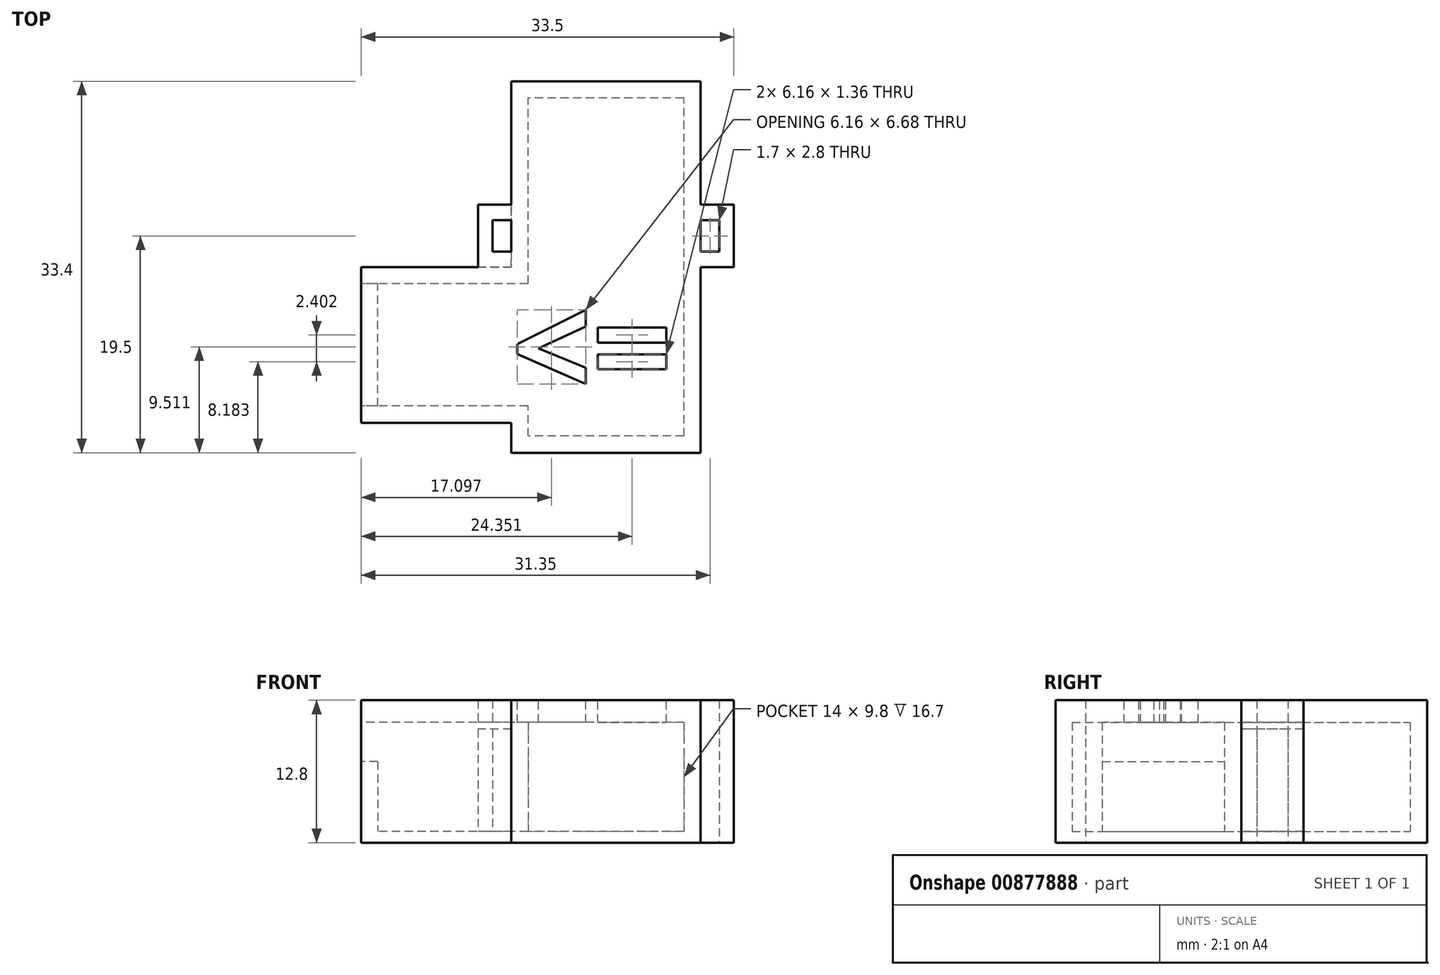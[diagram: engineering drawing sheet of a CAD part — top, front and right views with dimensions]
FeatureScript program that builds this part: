
annotation { "Feature Type Name" : "Feature", "Feature Type Description" : "" }
export const myFeature = defineFeature(function(context is Context, id is Id, definition is map)
    precondition{}
    {
        {
            var Q0;
            Q0=qCreatedBy(makeId("Top.planeOp"),FACE);
            var sketch = newSketch(context, id + "F0", { "sketchPlane" : qUnion([Q0])});
            skLineSegment(sketch, "E0.bottom", {"start": v(7, -15.2) * mm, "end": v(-7, -15.2) * mm});
            skLineSegment(sketch, "E0.top", {"start": v(7, 15.2) * mm, "end": v(-7, 15.2) * mm});
            skLineSegment(sketch, "E0.left", {"start": v(7, -15.2) * mm, "end": v(7, 15.2) * mm});
            skLineSegment(sketch, "E0.right", {"start": v(-7, -15.2) * mm, "end": v(-7, -12.5) * mm});
            skPoint(sketch, "E0.middle", {"position": v(0, 0) * mm});
            skLineSegment(sketch, "E1.bottom", {"start": v(-7, -12.5) * mm, "end": v(-20.5, -12.5) * mm});
            skLineSegment(sketch, "E1.top", {"start": v(-7, -1.5) * mm, "end": v(-20.5, -1.5) * mm});
            skLineSegment(sketch, "E1.right", {"start": v(-20.5, -12.5) * mm, "end": v(-20.5, -1.5) * mm});
            skLineSegment(sketch, "E2.trimOffspring", {"start": v(-7, -1.5) * mm, "end": v(-7, 15.2) * mm});
            skLineSegment(sketch, "E3.0", {"start": v(-8.5, 0) * mm, "end": v(-22, 0) * mm});
            skLineSegment(sketch, "E3.1", {"start": v(-22, -14) * mm, "end": v(-22, 0) * mm});
            skLineSegment(sketch, "E3.2", {"start": v(-8.5, 0) * mm, "end": v(-8.5, 16.7) * mm});
            skLineSegment(sketch, "E3.3", {"start": v(-8.5, -14) * mm, "end": v(-22, -14) * mm});
            skLineSegment(sketch, "E3.4", {"start": v(8.5, 16.7) * mm, "end": v(-8.5, 16.7) * mm});
            skLineSegment(sketch, "E3.5", {"start": v(8.5, -16.7) * mm, "end": v(8.5, 16.7) * mm});
            skLineSegment(sketch, "E3.6", {"start": v(8.5, -16.7) * mm, "end": v(-8.5, -16.7) * mm});
            skLineSegment(sketch, "E3.7", {"start": v(-8.5, -16.7) * mm, "end": v(-8.5, -14) * mm});
            skLineSegment(sketch, "E4.0", {"start": v(-7.75, -0.75) * mm, "end": v(-21.25, -0.75) * mm});
            skLineSegment(sketch, "E4.1", {"start": v(-21.25, -13.25) * mm, "end": v(-21.25, -0.75) * mm});
            skLineSegment(sketch, "E4.2", {"start": v(-7.75, -0.75) * mm, "end": v(-7.75, 15.95) * mm});
            skLineSegment(sketch, "E4.3", {"start": v(-7.75, -13.25) * mm, "end": v(-21.25, -13.25) * mm});
            skLineSegment(sketch, "E4.4", {"start": v(7.75, 15.95) * mm, "end": v(-7.75, 15.95) * mm});
            skLineSegment(sketch, "E4.5", {"start": v(7.75, -15.95) * mm, "end": v(7.75, 15.95) * mm});
            skLineSegment(sketch, "E4.6", {"start": v(7.75, -15.95) * mm, "end": v(-7.75, -15.95) * mm});
            skLineSegment(sketch, "E4.7", {"start": v(-7.75, -15.95) * mm, "end": v(-7.75, -13.25) * mm});
            skLineSegment(sketch, "E5.0", {"start": v(-8.5, 0) * mm, "end": v(-11.5, 0) * mm});
            skLineSegment(sketch, "E5.1", {"start": v(-11.5, 5.6) * mm, "end": v(-11.5, 0) * mm});
            skLineSegment(sketch, "E5.2", {"start": v(-8.5, 5.6) * mm, "end": v(-11.5, 5.6) * mm});
            skLineSegment(sketch, "E5.3", {"start": v(-8.5, 4.2) * mm, "end": v(-8.5, 5.6) * mm});
            skLineSegment(sketch, "E5.4", {"start": v(-8.5, 4.2) * mm, "end": v(-10.2, 4.2) * mm});
            skLineSegment(sketch, "E5.5", {"start": v(-10.2, 4.2) * mm, "end": v(-10.2, 1.4) * mm});
            skLineSegment(sketch, "E5.6", {"start": v(-8.5, 1.4) * mm, "end": v(-10.2, 1.4) * mm});
            skLineSegment(sketch, "E5.7", {"start": v(-8.5, 0) * mm, "end": v(-8.5, 1.4) * mm});
            skLineSegment(sketch, "E6.MirrorCS", {"start": v(8.5, 4.2) * mm, "end": v(10.2, 4.2) * mm});
            skLineSegment(sketch, "E7.MirrorCS", {"start": v(10.2, 4.2) * mm, "end": v(10.2, 1.4) * mm});
            skLineSegment(sketch, "E8.MirrorCS", {"start": v(8.5, 1.4) * mm, "end": v(10.2, 1.4) * mm});
            skLineSegment(sketch, "E9.MirrorCS", {"start": v(11.5, 5.6) * mm, "end": v(11.5, 0) * mm});
            skLineSegment(sketch, "E10.MirrorCS", {"start": v(8.5, 5.6) * mm, "end": v(11.5, 5.6) * mm});
            skLineSegment(sketch, "E11", {"start": v(11.5, 0) * mm, "end": v(8.5, 0) * mm});
            skSolve(sketch);
        }
        {
            var Q0;
            Q0 = qSketchRegion(id + "F0", true);
            var Q1;
            Q1=makeQuery(id+"F0.imprint","IMPRINT",FACE,{"disambiguationData":[TD([[makeQuery(id+"F0.imprint","IMPRINT",EDGE,{"derivedFrom":sQuery(id+"F0.wireOp",EDGE,"E0.bottom")}),1.0]])]});
            extrude(context, id + "F1", {"entities" : qUnion([Q0, Q1]), "depth" : 9.2 * mm, "offsetDistance" : 25 * mm});
        }
        {
            var Q0;
            Q0=makeQuery(id+"F0.imprint","IMPRINT",FACE,{"disambiguationData":[TD([[makeQuery(id+"F0.imprint","IMPRINT",EDGE,{"derivedFrom":sQuery(id+"F0.wireOp",EDGE,"E0.bottom")}),-1.0]])]});
            var Q1;
            Q1=makeQuery(id+"F0.imprint","IMPRINT",FACE,{"disambiguationData":[TD([[makeQuery(id+"F0.imprint","IMPRINT",EDGE,{"derivedFrom":sQuery(id+"F0.wireOp",EDGE,"E0.bottom")}),1.0]])]});
            var Q2;
            Q2=makeQuery(id+"F0.imprint","IMPRINT",FACE,{"disambiguationData":[TD([[makeQuery(id+"F0.imprint","IMPRINT",EDGE,{"derivedFrom":sQuery(id+"F0.wireOp",EDGE,"E3.0")}),1.0]])]});
            extrude(context, id + "F2", {"entities" : qUnion([Q0, Q1, Q2]), "operationType" : NewBodyOperationType.ADD, "oppositeDirection" : true, "depth" : 1 * mm, "offsetDistance" : 25 * mm});
        }
        {
            var Q0;
            Q0=makeQuery(id+"F0.imprint","IMPRINT",FACE,{"disambiguationData":[TD([[makeQuery(id+"F0.imprint","IMPRINT",EDGE,{"derivedFrom":sQuery(id+"F0.wireOp",EDGE,"E3.0")}),1.0]])]});
            var Q1;
            {var subQ0=sQuery(id+"F0.wireOp",EDGE,"E6.MirrorCS");Q1=makeQuery(id+"F0.imprint","IMPRINT",FACE,{"disambiguationData":[TD([[makeQuery(id+"F0.imprint","IMPRINT",EDGE,{"derivedFrom":subQ0}),1.0]])]});}
            var Q2;
            Q2=makeQuery(id+"F0.imprint","IMPRINT",FACE,{"disambiguationData":[TD([[makeQuery(id+"F0.imprint","IMPRINT",EDGE,{"derivedFrom":sQuery(id+"F0.wireOp",EDGE,"E5.0")}),-1.0]])]});
            extrude(context, id + "F3", {"entities" : qUnion([Q0, Q1, Q2]), "operationType" : NewBodyOperationType.ADD, "depth" : 9.8 * mm, "offsetDistance" : 25 * mm});
        }
        {
            var Q0;
            Q0=makeQuery(id+"F1.opExtrude","CAP_FACE",FACE,{"disambiguationData":[OSD([sQuery(id+"F0.wireOp",EDGE,"E0.bottom"),sQuery(id+"F0.wireOp",EDGE,"E0.top"),sQuery(id+"F0.wireOp",EDGE,"E0.left"),sQuery(id+"F0.wireOp",EDGE,"E0.right"),sQuery(id+"F0.wireOp",EDGE,"E1.bottom"),sQuery(id+"F0.wireOp",EDGE,"E1.top"),sQuery(id+"F0.wireOp",EDGE,"E1.right"),sQuery(id+"F0.wireOp",EDGE,"E2.trimOffspring"),sQuery(id+"F0.wireOp",EDGE,"E3.0"),sQuery(id+"F0.wireOp",EDGE,"E3.1"),sQuery(id+"F0.wireOp",EDGE,"E3.2"),sQuery(id+"F0.wireOp",EDGE,"E3.3"),sQuery(id+"F0.wireOp",EDGE,"E3.4"),sQuery(id+"F0.wireOp",EDGE,"E3.5"),sQuery(id+"F0.wireOp",EDGE,"E3.6"),sQuery(id+"F0.wireOp",EDGE,"E3.7"),sQuery(id+"F0.wireOp",EDGE,"E5.1"),sQuery(id+"F0.wireOp",EDGE,"E5.2"),sQuery(id+"F0.wireOp",EDGE,"E5.4"),sQuery(id+"F0.wireOp",EDGE,"E5.5"),sQuery(id+"F0.wireOp",EDGE,"E5.6"),sQuery(id+"F0.wireOp",EDGE,"E6.MirrorCS"),sQuery(id+"F0.wireOp",EDGE,"E7.MirrorCS"),sQuery(id+"F0.wireOp",EDGE,"E8.MirrorCS"),sQuery(id+"F0.wireOp",EDGE,"E9.MirrorCS"),sQuery(id+"F0.wireOp",EDGE,"E10.MirrorCS"),sQuery(id+"F0.wireOp",EDGE,"E11")])],"isStart":false});
            var sketch = newSketch(context, id + "F4", { "sketchPlane" : qUnion([Q0])});
            skLineSegment(sketch, "E12.0", {"start": v(-7.75, -0.75) * mm, "end": v(-21.25, -0.75) * mm});
            skLineSegment(sketch, "E12.1", {"start": v(-7.75, -0.75) * mm, "end": v(-7.75, 15.95) * mm});
            skLineSegment(sketch, "E12.2", {"start": v(-21.25, -13.25) * mm, "end": v(-21.25, -0.75) * mm});
            skLineSegment(sketch, "E12.3", {"start": v(-7.75, -13.25) * mm, "end": v(-21.25, -13.25) * mm});
            skLineSegment(sketch, "E12.4", {"start": v(-7.75, -15.95) * mm, "end": v(-7.75, -13.25) * mm});
            skLineSegment(sketch, "E12.5", {"start": v(7.75, -15.95) * mm, "end": v(-7.75, -15.95) * mm});
            skLineSegment(sketch, "E12.6", {"start": v(7.75, -15.95) * mm, "end": v(7.75, 15.95) * mm});
            skLineSegment(sketch, "E12.7", {"start": v(7.75, 15.95) * mm, "end": v(-7.75, 15.95) * mm});
            skLineSegment(sketch, "E13.0", {"start": v(-7, -1.5) * mm, "end": v(-7, 15.2) * mm});
            skLineSegment(sketch, "E13.1", {"start": v(7, 15.2) * mm, "end": v(-7, 15.2) * mm});
            skLineSegment(sketch, "E13.2", {"start": v(7, -15.2) * mm, "end": v(7, 15.2) * mm});
            skLineSegment(sketch, "E13.3", {"start": v(-7, -1.5) * mm, "end": v(-20.5, -1.5) * mm});
            skLineSegment(sketch, "E13.4", {"start": v(-20.5, -12.5) * mm, "end": v(-20.5, -1.5) * mm});
            skLineSegment(sketch, "E13.5", {"start": v(-7, -12.5) * mm, "end": v(-20.5, -12.5) * mm});
            skLineSegment(sketch, "E13.6", {"start": v(-7, -15.2) * mm, "end": v(-7, -12.5) * mm});
            skLineSegment(sketch, "E13.7", {"start": v(7, -15.2) * mm, "end": v(-7, -15.2) * mm});
            skSolve(sketch);
        }
        {
            var Q0;
            Q0 = qSketchRegion(id + "F4", true);
            var Q1;
            Q1=makeQuery(id+"F3.opExtrude","CAP_FACE",FACE,{"disambiguationData":[OSD([sQuery(id+"F0.wireOp",EDGE,"E3.0"),sQuery(id+"F0.wireOp",EDGE,"E3.1"),sQuery(id+"F0.wireOp",EDGE,"E3.2"),sQuery(id+"F0.wireOp",EDGE,"E3.3"),sQuery(id+"F0.wireOp",EDGE,"E3.4"),sQuery(id+"F0.wireOp",EDGE,"E3.5"),sQuery(id+"F0.wireOp",EDGE,"E3.6"),sQuery(id+"F0.wireOp",EDGE,"E3.7"),sQuery(id+"F0.wireOp",EDGE,"E4.0"),sQuery(id+"F0.wireOp",EDGE,"E4.1"),sQuery(id+"F0.wireOp",EDGE,"E4.2"),sQuery(id+"F0.wireOp",EDGE,"E4.3"),sQuery(id+"F0.wireOp",EDGE,"E4.4"),sQuery(id+"F0.wireOp",EDGE,"E4.5"),sQuery(id+"F0.wireOp",EDGE,"E4.6"),sQuery(id+"F0.wireOp",EDGE,"E4.7"),sQuery(id+"F0.wireOp",EDGE,"E5.1"),sQuery(id+"F0.wireOp",EDGE,"E5.2"),sQuery(id+"F0.wireOp",EDGE,"E5.4"),sQuery(id+"F0.wireOp",EDGE,"E5.5"),sQuery(id+"F0.wireOp",EDGE,"E5.6"),sQuery(id+"F0.wireOp",EDGE,"E6.MirrorCS"),sQuery(id+"F0.wireOp",EDGE,"E7.MirrorCS"),sQuery(id+"F0.wireOp",EDGE,"E8.MirrorCS"),sQuery(id+"F0.wireOp",EDGE,"E9.MirrorCS"),sQuery(id+"F0.wireOp",EDGE,"E10.MirrorCS"),sQuery(id+"F0.wireOp",EDGE,"E11")])],"isStart":false});
            extrude(context, id + "F5", {"entities" : qUnion([Q0]), "endBound" : BoundingType.UP_TO_SURFACE, "depth" : 25 * mm, "endBoundEntityFace" : qUnion([Q1]), "offsetDistance" : 25 * mm});
        }
        {
            var Q0;
            Q0=makeQuery(id+"F5.opExtrude","CAP_FACE",FACE,{"disambiguationData":[OSD([sQuery(id+"F4.wireOp",EDGE,"E12.0"),sQuery(id+"F4.wireOp",EDGE,"E12.1"),sQuery(id+"F4.wireOp",EDGE,"E12.2"),sQuery(id+"F4.wireOp",EDGE,"E12.3"),sQuery(id+"F4.wireOp",EDGE,"E12.4"),sQuery(id+"F4.wireOp",EDGE,"E12.5"),sQuery(id+"F4.wireOp",EDGE,"E12.6"),sQuery(id+"F4.wireOp",EDGE,"E12.7"),sQuery(id+"F4.wireOp",EDGE,"E13.0"),sQuery(id+"F4.wireOp",EDGE,"E13.1"),sQuery(id+"F4.wireOp",EDGE,"E13.2"),sQuery(id+"F4.wireOp",EDGE,"E13.3"),sQuery(id+"F4.wireOp",EDGE,"E13.4"),sQuery(id+"F4.wireOp",EDGE,"E13.5"),sQuery(id+"F4.wireOp",EDGE,"E13.6"),sQuery(id+"F4.wireOp",EDGE,"E13.7")])],"isStart":false});
            var sketch = newSketch(context, id + "F6", { "sketchPlane" : qUnion([Q0])});
            skLineSegment(sketch, "E14.0", {"start": v(-8.5, 0) * mm, "end": v(-22, 0) * mm});
            skLineSegment(sketch, "E14.1", {"start": v(-22, -14) * mm, "end": v(-22, 0) * mm});
            skLineSegment(sketch, "E14.2", {"start": v(-8.5, -14) * mm, "end": v(-22, -14) * mm});
            skLineSegment(sketch, "E14.3", {"start": v(-8.5, -16.7) * mm, "end": v(-8.5, -14) * mm});
            skLineSegment(sketch, "E14.4", {"start": v(8.5, -16.7) * mm, "end": v(-8.5, -16.7) * mm});
            skLineSegment(sketch, "E14.5", {"start": v(8.5, -16.7) * mm, "end": v(8.5, 16.7) * mm});
            skLineSegment(sketch, "E14.6", {"start": v(11.5, 0) * mm, "end": v(8.5, 0) * mm});
            skLineSegment(sketch, "E14.7", {"start": v(11.5, 5.6) * mm, "end": v(11.5, 0) * mm});
            skLineSegment(sketch, "E14.8", {"start": v(8.5, 5.6) * mm, "end": v(11.5, 5.6) * mm});
            skLineSegment(sketch, "E14.9", {"start": v(8.5, 4.2) * mm, "end": v(10.2, 4.2) * mm});
            skLineSegment(sketch, "E14.10", {"start": v(10.2, 4.2) * mm, "end": v(10.2, 1.4) * mm});
            skLineSegment(sketch, "E14.11", {"start": v(8.5, 1.4) * mm, "end": v(10.2, 1.4) * mm});
            skLineSegment(sketch, "E14.12", {"start": v(-8.5, 1.4) * mm, "end": v(-10.2, 1.4) * mm});
            skLineSegment(sketch, "E14.13", {"start": v(-8.5, 4.2) * mm, "end": v(-10.2, 4.2) * mm});
            skLineSegment(sketch, "E14.14", {"start": v(-10.2, 4.2) * mm, "end": v(-10.2, 1.4) * mm});
            skLineSegment(sketch, "E14.15", {"start": v(-8.5, 0) * mm, "end": v(-8.5, 16.7) * mm});
            skLineSegment(sketch, "E14.16", {"start": v(-11.5, 5.6) * mm, "end": v(-11.5, 0) * mm});
            skLineSegment(sketch, "E14.17", {"start": v(-8.5, 5.6) * mm, "end": v(-11.5, 5.6) * mm});
            skLineSegment(sketch, "E14.18", {"start": v(8.5, 16.7) * mm, "end": v(-8.5, 16.7) * mm});
            skSolve(sketch);
        }
        {
            var Q0;
            Q0 = qSketchRegion(id + "F6", true);
            extrude(context, id + "F7", {"entities" : qUnion([Q0]), "operationType" : NewBodyOperationType.ADD, "depth" : 2 * mm, "offsetDistance" : 25 * mm});
        }
        {
            var Q0;
            {var subQ0=sQuery(id+"F0.wireOp",EDGE,"E3.1");Q0=makeQuery(id+"F3.boolean.opBoolean","MERGE",FACE,{"derivedFrom":[makeQuery(id+"F2.boolean.opBoolean","MERGE",FACE,{"derivedFrom":[makeQuery(id+"F1.opExtrude","SWEPT_FACE",FACE,{"disambiguationData":[OSD([subQ0])]}),makeQuery(id+"F2.opExtrude","SWEPT_FACE",FACE,{"disambiguationData":[OSD([subQ0])]})]}),makeQuery(id+"F3.opExtrude","SWEPT_FACE",FACE,{"disambiguationData":[OSD([subQ0])]})]});}
            var sketch = newSketch(context, id + "F8", { "sketchPlane" : qUnion([Q0])});
            skLineSegment(sketch, "E15.bottom", {"start": v(1.5, 9) * mm, "end": v(12.5, 9) * mm});
            skLineSegment(sketch, "E15.top", {"start": v(1.5, 6.3) * mm, "end": v(12.5, 6.3) * mm});
            skLineSegment(sketch, "E15.left", {"start": v(1.5, 9) * mm, "end": v(1.5, 6.3) * mm});
            skLineSegment(sketch, "E15.right", {"start": v(12.5, 9) * mm, "end": v(12.5, 6.3) * mm});
            skLineSegment(sketch, "E16.top", {"start": v(1.5, 9.8) * mm, "end": v(12.5, 9.8) * mm});
            skLineSegment(sketch, "E16.left", {"start": v(1.5, 9) * mm, "end": v(1.5, 9.8) * mm});
            skLineSegment(sketch, "E16.right", {"start": v(12.5, 9) * mm, "end": v(12.5, 9.8) * mm});
            skSolve(sketch);
        }
        {
            var Q0;
            Q0 = qSketchRegion(id + "F8", true);
            var Q1;
            Q1=makeQuery(id+"F1.opExtrude","SWEPT_FACE",FACE,{"disambiguationData":[OSD([sQuery(id+"F0.wireOp",EDGE,"E1.right")])]});
            extrude(context, id + "F9", {"entities" : qUnion([Q0]), "operationType" : NewBodyOperationType.REMOVE, "endBound" : BoundingType.UP_TO_SURFACE, "oppositeDirection" : true, "depth" : 25 * mm, "endBoundEntityFace" : qUnion([Q1]), "offsetDistance" : 25 * mm});
        }
        {
            var Q0;
            Q0=makeQuery(id+"F7.opExtrude","CAP_FACE",FACE,{"disambiguationData":[OSD([sQuery(id+"F6.wireOp",EDGE,"E14.0"),sQuery(id+"F6.wireOp",EDGE,"E14.1"),sQuery(id+"F6.wireOp",EDGE,"E14.2"),sQuery(id+"F6.wireOp",EDGE,"E14.3"),sQuery(id+"F6.wireOp",EDGE,"E14.4"),sQuery(id+"F6.wireOp",EDGE,"E14.5"),sQuery(id+"F6.wireOp",EDGE,"E14.6"),sQuery(id+"F6.wireOp",EDGE,"E14.7"),sQuery(id+"F6.wireOp",EDGE,"E14.8"),sQuery(id+"F6.wireOp",EDGE,"E14.9"),sQuery(id+"F6.wireOp",EDGE,"E14.10"),sQuery(id+"F6.wireOp",EDGE,"E14.11"),sQuery(id+"F6.wireOp",EDGE,"E14.12"),sQuery(id+"F6.wireOp",EDGE,"E14.13"),sQuery(id+"F6.wireOp",EDGE,"E14.14"),sQuery(id+"F6.wireOp",EDGE,"E14.15"),sQuery(id+"F6.wireOp",EDGE,"E14.16"),sQuery(id+"F6.wireOp",EDGE,"E14.17"),sQuery(id+"F6.wireOp",EDGE,"E14.18")])],"isStart":false});
            var sketch = newSketch(context, id + "F10", { "sketchPlane" : qUnion([Q0])});
            skText(sketch, "E17", { "text": "<=", "fontName": "OpenSans-Bold.ttf"});
            const initialGuessF10  = {"E17": [-0.00853, -0.01179, 1, 0, 0.00915]};
            skSetInitialGuess(sketch, initialGuessF10);
            skSolve(sketch);
        }
        {
            var Q0;
            Q0 = qSketchRegion(id + "F10", true);
            var Q1;
            Q1=makeQuery(id+"F7.boolean.opBoolean","SPLIT",FACE,{"disambiguationData":[TD([makeQuery(id+"F5.opExtrude","SWEPT_FACE",FACE,{"disambiguationData":[OSD([sQuery(id+"F4.wireOp",EDGE,"E13.0")])]})])],"derivedFrom":makeQuery(id+"F7.opExtrude","CAP_FACE",FACE,{"disambiguationData":[OSD([sQuery(id+"F6.wireOp",EDGE,"E14.0"),sQuery(id+"F6.wireOp",EDGE,"E14.1"),sQuery(id+"F6.wireOp",EDGE,"E14.2"),sQuery(id+"F6.wireOp",EDGE,"E14.3"),sQuery(id+"F6.wireOp",EDGE,"E14.4"),sQuery(id+"F6.wireOp",EDGE,"E14.5"),sQuery(id+"F6.wireOp",EDGE,"E14.6"),sQuery(id+"F6.wireOp",EDGE,"E14.7"),sQuery(id+"F6.wireOp",EDGE,"E14.8"),sQuery(id+"F6.wireOp",EDGE,"E14.9"),sQuery(id+"F6.wireOp",EDGE,"E14.10"),sQuery(id+"F6.wireOp",EDGE,"E14.11"),sQuery(id+"F6.wireOp",EDGE,"E14.12"),sQuery(id+"F6.wireOp",EDGE,"E14.13"),sQuery(id+"F6.wireOp",EDGE,"E14.14"),sQuery(id+"F6.wireOp",EDGE,"E14.15"),sQuery(id+"F6.wireOp",EDGE,"E14.16"),sQuery(id+"F6.wireOp",EDGE,"E14.17"),sQuery(id+"F6.wireOp",EDGE,"E14.18")])],"isStart":true})});
            extrude(context, id + "F11", {"entities" : qUnion([Q0]), "operationType" : NewBodyOperationType.REMOVE, "endBound" : BoundingType.UP_TO_SURFACE, "oppositeDirection" : true, "depth" : 25 * mm, "endBoundEntityFace" : qUnion([Q1]), "offsetDistance" : 25 * mm});
        }
        {
            var Q0;
            Q0=makeQuery(id+"F0.imprint","IMPRINT",FACE,{"disambiguationData":[TD([[makeQuery(id+"F0.imprint","IMPRINT",EDGE,{"derivedFrom":sQuery(id+"F0.wireOp",EDGE,"E5.0")}),-1.0]])]});
            var Q1;
            {var subQ0=sQuery(id+"F0.wireOp",EDGE,"E6.MirrorCS");Q1=makeQuery(id+"F0.imprint","IMPRINT",FACE,{"disambiguationData":[TD([[makeQuery(id+"F0.imprint","IMPRINT",EDGE,{"derivedFrom":subQ0}),1.0]])]});}
            var Q2;
            Q2=makeQuery(id+"F2.opExtrude","CAP_FACE",FACE,{"disambiguationData":[OSD([sQuery(id+"F0.wireOp",EDGE,"E3.0"),sQuery(id+"F0.wireOp",EDGE,"E3.1"),sQuery(id+"F0.wireOp",EDGE,"E3.2"),sQuery(id+"F0.wireOp",EDGE,"E3.3"),sQuery(id+"F0.wireOp",EDGE,"E3.4"),sQuery(id+"F0.wireOp",EDGE,"E3.5"),sQuery(id+"F0.wireOp",EDGE,"E3.6"),sQuery(id+"F0.wireOp",EDGE,"E3.7"),sQuery(id+"F0.wireOp",EDGE,"E5.0"),sQuery(id+"F0.wireOp",EDGE,"E5.3"),sQuery(id+"F0.wireOp",EDGE,"E5.7")])],"isStart":false});
            extrude(context, id + "F12", {"entities" : qUnion([Q0, Q1]), "operationType" : NewBodyOperationType.ADD, "endBound" : BoundingType.UP_TO_SURFACE, "oppositeDirection" : true, "depth" : 25 * mm, "endBoundEntityFace" : qUnion([Q2]), "offsetDistance" : 25 * mm});
        }
    });
